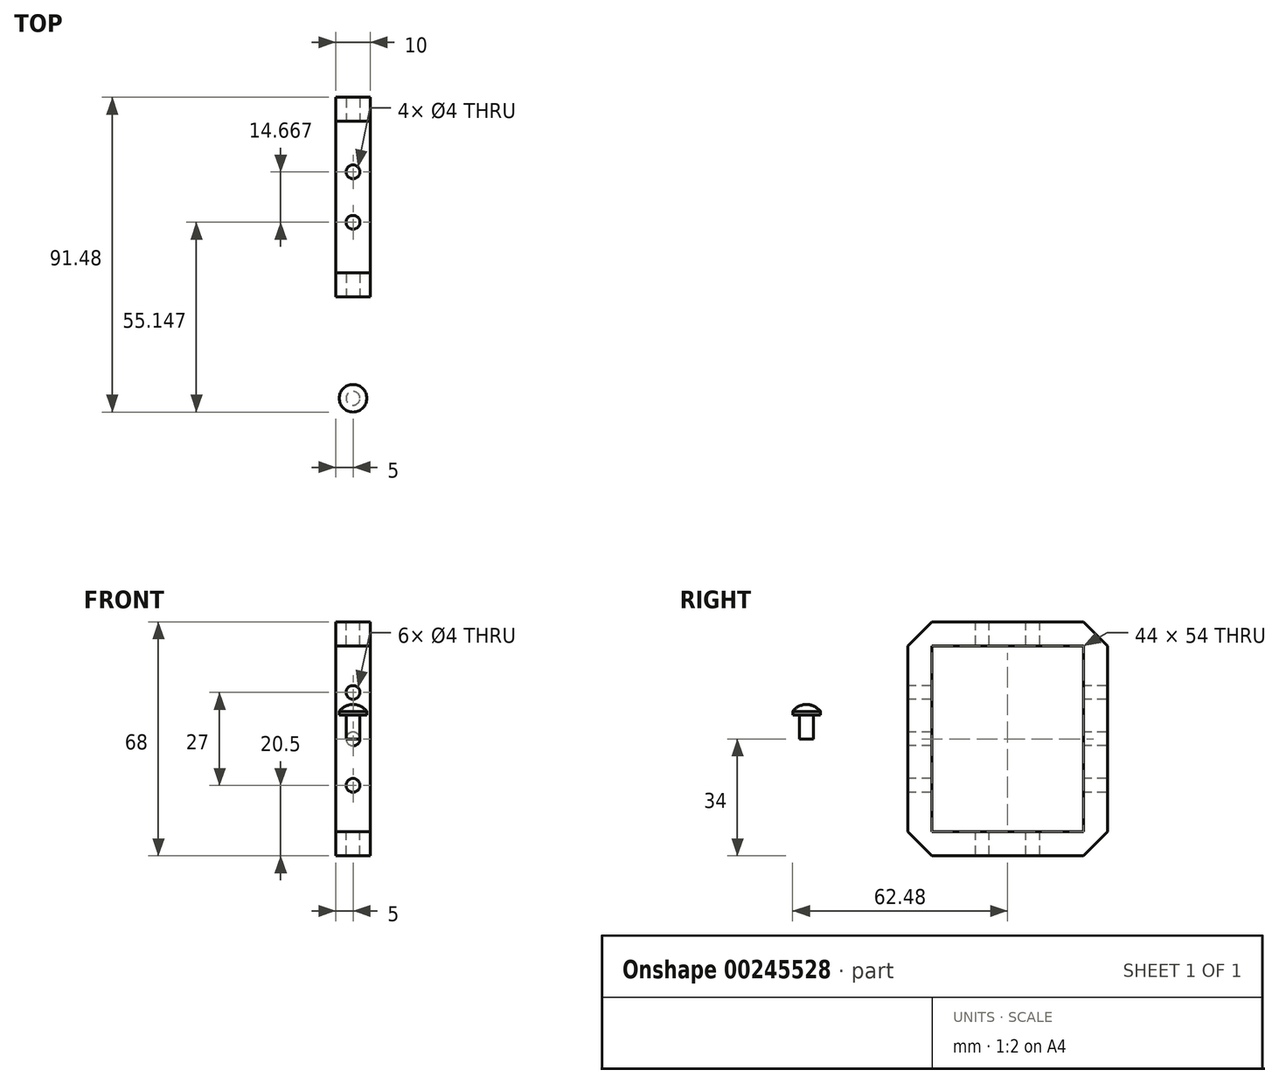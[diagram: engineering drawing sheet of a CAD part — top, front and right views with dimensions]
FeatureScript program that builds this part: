
annotation { "Feature Type Name" : "Feature", "Feature Type Description" : "" }
export const myFeature = defineFeature(function(context is Context, id is Id, definition is map)
    precondition{}
    {
        {
            var Q0;
            Q0=qCreatedBy(makeId("Right.planeOp"),FACE);
            var sketch = newSketch(context, id + "F0", { "sketchPlane" : qUnion([Q0])});
            skLineSegment(sketch, "E0.bottom", {"start": v(-22, 27) * mm, "end": v(22, 27) * mm});
            skLineSegment(sketch, "E0.top", {"start": v(-22, -27) * mm, "end": v(22, -27) * mm});
            skLineSegment(sketch, "E0.left", {"start": v(-22, 27) * mm, "end": v(-22, -27) * mm});
            skLineSegment(sketch, "E0.right", {"start": v(22, 27) * mm, "end": v(22, -27) * mm});
            skPoint(sketch, "E0.middle", {"position": v(0, 0) * mm});
            skLineSegment(sketch, "E1", {"start": v(-22, 34) * mm, "end": v(22, 34) * mm});
            skLineSegment(sketch, "E2", {"start": v(22, 34) * mm, "end": v(29, 27) * mm});
            skLineSegment(sketch, "E3", {"start": v(29, 27) * mm, "end": v(29, -27) * mm});
            skLineSegment(sketch, "E4", {"start": v(29, -27) * mm, "end": v(22, -34) * mm});
            skLineSegment(sketch, "E5", {"start": v(22, -34) * mm, "end": v(-22, -34) * mm});
            skLineSegment(sketch, "E6", {"start": v(-22, -34) * mm, "end": v(-29, -27) * mm});
            skLineSegment(sketch, "E7", {"start": v(-29, -27) * mm, "end": v(-29, 27) * mm});
            skLineSegment(sketch, "E8", {"start": v(-29, 27) * mm, "end": v(-22, 34) * mm});
            skLineSegment(sketch, "E9", {"start": v(-22, 0) * mm, "end": v(-29, 0) * mm, "construction": true});
            skLineSegment(sketch, "E10", {"start": v(0, 27) * mm, "end": v(0, 34) * mm, "construction": true});
            skLineSegment(sketch, "E11", {"start": v(22, 0) * mm, "end": v(29, 0) * mm, "construction": true});
            skLineSegment(sketch, "E12", {"start": v(0, -27) * mm, "end": v(0, -34) * mm, "construction": true});
            skLineSegment(sketch, "E13", {"start": v(-58.48, 24.23) * mm, "end": v(-58.48, -36.75) * mm, "construction": true});
            skLineSegment(sketch, "E14", {"start": v(-58.48, 0) * mm, "end": v(-60.48, 0) * mm});
            skLineSegment(sketch, "E15", {"start": v(-60.48, 0) * mm, "end": v(-60.48, 7) * mm});
            skLineSegment(sketch, "E16", {"start": v(-60.48, 7) * mm, "end": v(-62.48, 7) * mm});
            skLineSegment(sketch, "E17", {"start": v(-62.48, 7) * mm, "end": v(-62.48, 8) * mm});
            skLineSegment(sketch, "E18", {"start": v(-58.48, 0) * mm, "end": v(-58.48, 10) * mm});
            skArc(sketch, "E19", {"start": v(-58.48, 10) * mm, "mid": v(-60.71, 9.47) * mm, "end": v(-62.48, 8) * mm});
            skSolve(sketch);
        }
        {
            var Q0;
            Q0=makeQuery(id+"F0.imprint","IMPRINT",FACE,{"disambiguationData":[TD([[makeQuery(id+"F0.imprint","IMPRINT",EDGE,{"derivedFrom":sQuery(id+"F0.wireOp",EDGE,"E0.bottom")}),1.0]])]});
            extrude(context, id + "F1", {"entities" : qUnion([Q0]), "endBound" : BoundingType.SYMMETRIC, "depth" : 10 * mm});
        }
        {
            var Q0;
            Q0=qCreatedBy(makeId("Top.planeOp"),FACE);
            var sketch = newSketch(context, id + "F2", { "sketchPlane" : qUnion([Q0])});
            skLineSegment(sketch, "E20", {"start": v(-20, 22) * mm, "end": v(0, 22) * mm, "construction": true});
            skLineSegment(sketch, "E21", {"start": v(0, 22) * mm, "end": v(0, 7.33) * mm, "construction": true});
            skLineSegment(sketch, "E22", {"start": v(0, 7.33) * mm, "end": v(-15, 7.33) * mm, "construction": true});
            skLineSegment(sketch, "E23", {"start": v(-15, 7.33) * mm, "end": v(-15, -7.33) * mm, "construction": true});
            skLineSegment(sketch, "E24", {"start": v(-15, -7.33) * mm, "end": v(0, -7.33) * mm, "construction": true});
            skLineSegment(sketch, "E25", {"start": v(0, -7.33) * mm, "end": v(0, -22) * mm, "construction": true});
            skLineSegment(sketch, "E26", {"start": v(0, -22) * mm, "end": v(-20, -22) * mm, "construction": true});
            skLineSegment(sketch, "E27", {"start": v(-20, -22) * mm, "end": v(-20, 22) * mm, "construction": true});
            skCircle(sketch, "E28", {"center": v(0, 7.33) * mm, "radius": 2 * mm});
            skCircle(sketch, "E29", {"center": v(0, -7.33) * mm, "radius": 2 * mm});
            skSolve(sketch);
        }
        {
            var Q0;
            Q0=makeQuery(id+"F2.imprint","IMPRINT",FACE,{"disambiguationData":[TD([[makeQuery(id+"F2.imprint","IMPRINT",EDGE,{"derivedFrom":sQuery(id+"F2.wireOp",EDGE,"E28")}),1.0]])]});
            var Q1;
            Q1=makeQuery(id+"F2.imprint","IMPRINT",FACE,{"disambiguationData":[TD([[makeQuery(id+"F2.imprint","IMPRINT",EDGE,{"derivedFrom":sQuery(id+"F2.wireOp",EDGE,"E29")}),1.0]])]});
            extrude(context, id + "F3", {"entities" : qUnion([Q0, Q1]), "operationType" : NewBodyOperationType.REMOVE, "endBound" : BoundingType.SYMMETRIC, "oppositeDirection" : true, "depth" : 88 * mm});
        }
        {
            var Q0;
            Q0=qCreatedBy(makeId("Front.planeOp"),FACE);
            var sketch = newSketch(context, id + "F4", { "sketchPlane" : qUnion([Q0])});
            skLineSegment(sketch, "E30", {"start": v(0, 0) * mm, "end": v(0, 13.5) * mm, "construction": true});
            skLineSegment(sketch, "E31", {"start": v(0, 13.5) * mm, "end": v(8.3, 13.5) * mm, "construction": true});
            skLineSegment(sketch, "E32", {"start": v(8.3, 13.5) * mm, "end": v(8.3, 27) * mm, "construction": true});
            skLineSegment(sketch, "E33", {"start": v(8.3, 27) * mm, "end": v(-14.66, 27) * mm, "construction": true});
            skLineSegment(sketch, "E34", {"start": v(-14.66, 27) * mm, "end": v(-14.66, -27) * mm, "construction": true});
            skLineSegment(sketch, "E35", {"start": v(-14.66, -27) * mm, "end": v(8.3, -27) * mm, "construction": true});
            skLineSegment(sketch, "E36", {"start": v(8.3, -27) * mm, "end": v(8.3, -13.5) * mm, "construction": true});
            skLineSegment(sketch, "E37", {"start": v(8.3, -13.5) * mm, "end": v(0, -13.5) * mm, "construction": true});
            skLineSegment(sketch, "E38", {"start": v(0, -13.5) * mm, "end": v(0, 0) * mm, "construction": true});
            skCircle(sketch, "E39", {"center": v(0, -13.5) * mm, "radius": 2 * mm});
            skCircle(sketch, "E40", {"center": v(0, 0) * mm, "radius": 2 * mm});
            skCircle(sketch, "E41", {"center": v(0, 13.5) * mm, "radius": 2 * mm});
            skSolve(sketch);
        }
        {
            var Q0;
            Q0 = qSketchRegion(id + "F4", true);
            var Q1;
            Q1=sQuery(id+"F4.wireOp",EDGE,"E30");
            var Q2;
            Q2=sQuery(id+"F4.wireOp",EDGE,"E31");
            var Q3;
            Q3=sQuery(id+"F4.wireOp",EDGE,"E32");
            var Q4;
            Q4=sQuery(id+"F4.wireOp",EDGE,"E33");
            var Q5;
            Q5=sQuery(id+"F4.wireOp",EDGE,"E34");
            var Q6;
            Q6=sQuery(id+"F4.wireOp",EDGE,"E35");
            var Q7;
            Q7=sQuery(id+"F4.wireOp",EDGE,"E38");
            var Q8;
            Q8=sQuery(id+"F4.wireOp",EDGE,"E37");
            var Q9;
            Q9=sQuery(id+"F4.wireOp",EDGE,"E36");
            extrude(context, id + "F5", {"entities" : qUnion([Q0]), "operationType" : NewBodyOperationType.REMOVE, "surfaceEntities" : qUnion([Q1, Q2, Q3, Q4, Q5, Q6, Q7, Q8, Q9]), "endBound" : BoundingType.SYMMETRIC, "oppositeDirection" : true, "depth" : 72.8 * mm});
        }
        {
            var Q0;
            Q0=makeQuery(id+"F0.imprint","IMPRINT",FACE,{"disambiguationData":[TD([[makeQuery(id+"F0.imprint","IMPRINT",EDGE,{"derivedFrom":sQuery(id+"F0.wireOp",EDGE,"E14")}),-1.0]])]});
            var Q1;
            Q1=sQuery(id+"F0.wireOp",EDGE,"E13");
            revolve(context, id + "F6", {"entities" : qUnion([Q0]), "axis" : qUnion([Q1]), "revolveType" : RevolveType.FULL});
        }
    });
